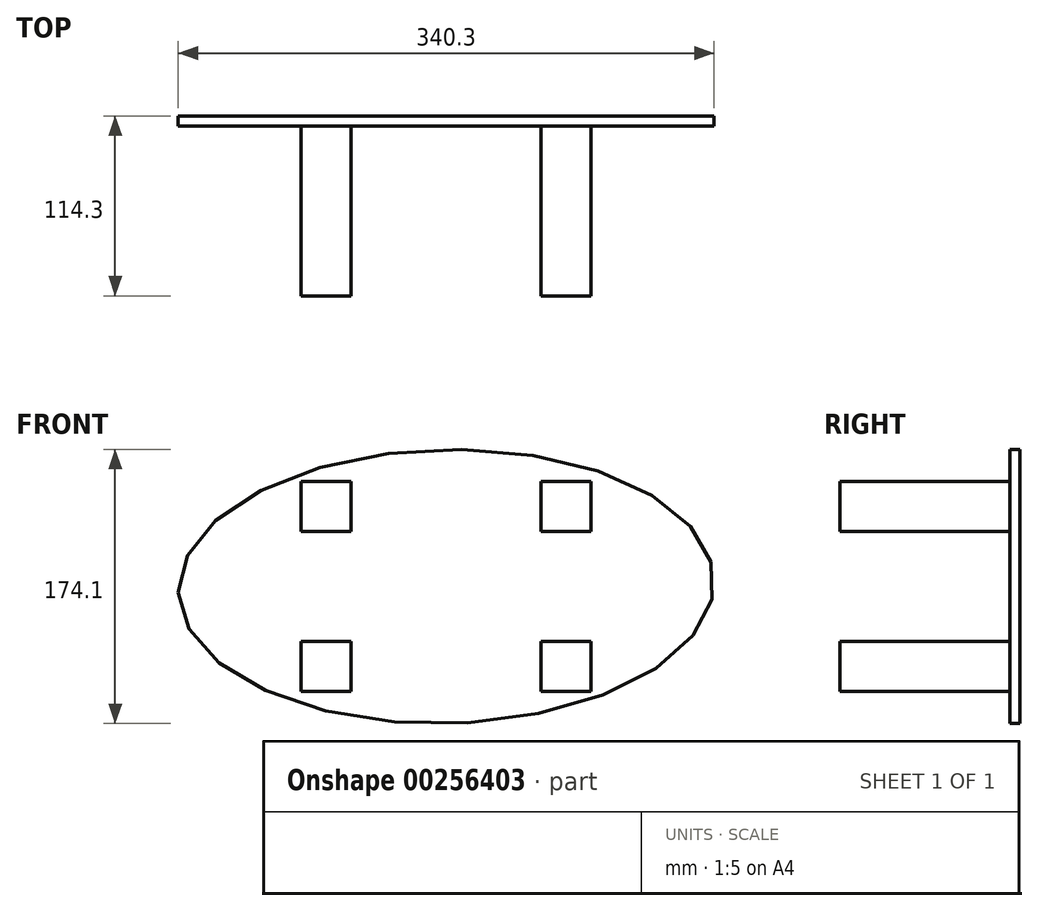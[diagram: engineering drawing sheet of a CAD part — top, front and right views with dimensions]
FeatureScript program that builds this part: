
annotation { "Feature Type Name" : "Feature", "Feature Type Description" : "" }
export const myFeature = defineFeature(function(context is Context, id is Id, definition is map)
    precondition{}
    {
        {
            var Q0;
            Q0=qCreatedBy(makeId("Front.planeOp"),FACE);
            var sketch = newSketch(context, id + "F0", { "sketchPlane" : qUnion([Q0])});
            skLineSegment(sketch, "E0", {"start": v(0, 0) * mm, "end": v(-76.2, 0) * mm});
            skLineSegment(sketch, "E1", {"start": v(0, 0) * mm, "end": v(76.2, 0) * mm});
            skLineSegment(sketch, "E2", {"start": v(76.2, 0) * mm, "end": v(76.2, -50.8) * mm});
            skLineSegment(sketch, "E3", {"start": v(76.2, 0) * mm, "end": v(76.2, 50.8) * mm});
            skLineSegment(sketch, "E4", {"start": v(-76.2, 0) * mm, "end": v(-76.2, 50.8) * mm});
            skLineSegment(sketch, "E5", {"start": v(-76.2, 0) * mm, "end": v(-76.2, -50.8) * mm});
            skLineSegment(sketch, "E6.bottom", {"start": v(-60.33, -34.93) * mm, "end": v(-92.08, -34.93) * mm});
            skLineSegment(sketch, "E6.top", {"start": v(-60.33, -66.67) * mm, "end": v(-92.08, -66.67) * mm});
            skLineSegment(sketch, "E6.left", {"start": v(-60.33, -34.93) * mm, "end": v(-60.33, -66.67) * mm});
            skLineSegment(sketch, "E6.right", {"start": v(-92.08, -34.93) * mm, "end": v(-92.08, -66.67) * mm});
            skPoint(sketch, "E6.middle", {"position": v(-76.2, -50.8) * mm});
            skLineSegment(sketch, "E7.bottom", {"start": v(-60.32, 66.67) * mm, "end": v(-92.08, 66.67) * mm});
            skLineSegment(sketch, "E7.top", {"start": v(-60.32, 34.92) * mm, "end": v(-92.07, 34.92) * mm});
            skLineSegment(sketch, "E7.left", {"start": v(-60.32, 66.67) * mm, "end": v(-60.32, 34.92) * mm});
            skLineSegment(sketch, "E7.right", {"start": v(-92.07, 66.67) * mm, "end": v(-92.07, 34.92) * mm});
            skPoint(sketch, "E7.middle", {"position": v(-76.2, 50.8) * mm});
            skLineSegment(sketch, "E8.bottom", {"start": v(92.08, 66.68) * mm, "end": v(60.33, 66.68) * mm});
            skLineSegment(sketch, "E8.top", {"start": v(92.08, 34.93) * mm, "end": v(60.33, 34.93) * mm});
            skLineSegment(sketch, "E8.left", {"start": v(92.08, 66.68) * mm, "end": v(92.08, 34.93) * mm});
            skLineSegment(sketch, "E8.right", {"start": v(60.33, 66.68) * mm, "end": v(60.33, 34.93) * mm});
            skPoint(sketch, "E8.middle", {"position": v(76.2, 50.8) * mm});
            skLineSegment(sketch, "E9.bottom", {"start": v(92.08, -34.92) * mm, "end": v(60.33, -34.92) * mm});
            skLineSegment(sketch, "E9.top", {"start": v(92.08, -66.67) * mm, "end": v(60.33, -66.67) * mm});
            skLineSegment(sketch, "E9.left", {"start": v(92.08, -34.92) * mm, "end": v(92.08, -66.67) * mm});
            skLineSegment(sketch, "E9.right", {"start": v(60.33, -34.92) * mm, "end": v(60.33, -66.67) * mm});
            skPoint(sketch, "E9.middle", {"position": v(76.2, -50.8) * mm});
            skSolve(sketch);
        }
        {
            var Q0;
            Q0=makeQuery(id+"F0.imprint","IMPRINT",FACE,{"disambiguationData":[TD([[makeQuery(id+"F0.imprint","IMPRINT",EDGE,{"derivedFrom":sQuery(id+"F0.wireOp",EDGE,"E7.bottom")}),1.0]])]});
            var Q1;
            Q1=makeQuery(id+"F0.imprint","IMPRINT",FACE,{"disambiguationData":[TD([[makeQuery(id+"F0.imprint","IMPRINT",EDGE,{"derivedFrom":sQuery(id+"F0.wireOp",EDGE,"E8.bottom")}),1.0]])]});
            var Q2;
            Q2=makeQuery(id+"F0.imprint","IMPRINT",FACE,{"disambiguationData":[TD([[makeQuery(id+"F0.imprint","IMPRINT",EDGE,{"derivedFrom":sQuery(id+"F0.wireOp",EDGE,"E9.top")}),-1.0]])]});
            var Q3;
            Q3=makeQuery(id+"F0.imprint","IMPRINT",FACE,{"disambiguationData":[TD([[makeQuery(id+"F0.imprint","IMPRINT",EDGE,{"derivedFrom":sQuery(id+"F0.wireOp",EDGE,"E6.top")}),-1.0]])]});
            extrude(context, id + "F1", {"entities" : qUnion([Q0, Q1, Q2, Q3]), "depth" : 107.95 * mm});
        }
        {
            var Q0;
            Q0=qCreatedBy(makeId("Front.planeOp"),FACE);
            var sketch = newSketch(context, id + "F2", { "sketchPlane" : qUnion([Q0])});
            skEllipse(sketch, "E10", {"center": v(0, 0) * mm, "majorRadius": 170.18 * mm, "minorRadius": 86.99 * mm, "majorAxis": v(-1, -0.02)});
            skSolve(sketch);
        }
        {
            var Q0;
            Q0=makeQuery(id+"F2.imprint","IMPRINT",FACE,{"disambiguationData":[TD([[makeQuery(id+"F2.imprint","IMPRINT",EDGE,{"derivedFrom":sQuery(id+"F2.wireOp",EDGE,"E10")}),1.0]])]});
            extrude(context, id + "F3", {"entities" : qUnion([Q0]), "oppositeDirection" : true, "depth" : 6.35 * mm});
        }
    });
